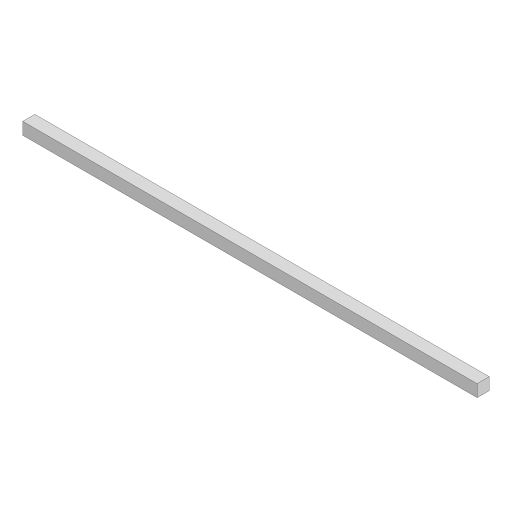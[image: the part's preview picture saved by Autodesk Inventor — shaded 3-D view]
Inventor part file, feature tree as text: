
AUTODESK INVENTOR PART (.ipt)
format: ipt  version: 2023 (Build 270158000, 158)  size: 77,824 bytes
history: native  units: mm
features: extrude x1, sketch x1
ambient origin geometry x8: Origin, YZ Plane, XZ Plane, XY Plane, X Axis, Y Axis, Z Axis, Center Point
bodies: 实体1 (feature_tree)
feature tree (2):
  extrude  "拉伸1"  Depth=20.0mm
  sketch  "草图1"  dims[d0=20.0mm d1=20.0mm d2=750.0mm d3=0.0mm]
